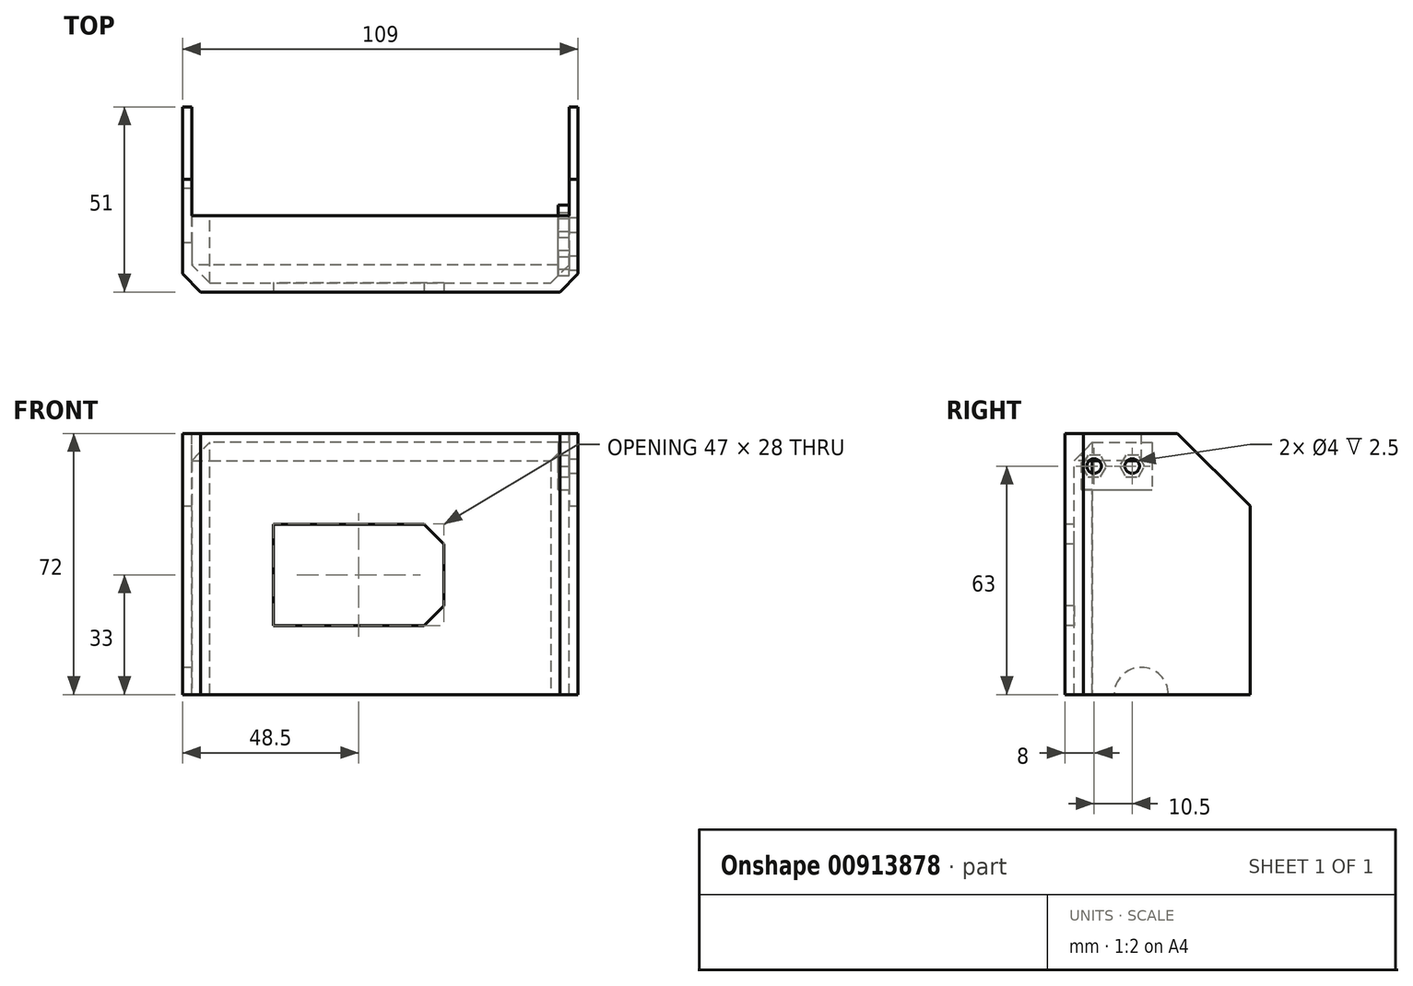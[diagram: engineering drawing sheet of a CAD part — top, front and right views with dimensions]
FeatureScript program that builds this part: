
annotation { "Feature Type Name" : "Feature", "Feature Type Description" : "" }
export const myFeature = defineFeature(function(context is Context, id is Id, definition is map)
    precondition{}
    {
        {
            var Q0;
            Q0=qCreatedBy(makeId("Front.planeOp"),FACE);
            var sketch = newSketch(context, id + "F0", { "sketchPlane" : qUnion([Q0])});
            skLineSegment(sketch, "E0.bottom", {"start": v(0, 0) * mm, "end": v(109, 0) * mm});
            skLineSegment(sketch, "E0.top", {"start": v(0, 72) * mm, "end": v(109, 72) * mm});
            skLineSegment(sketch, "E0.left", {"start": v(0, 0) * mm, "end": v(0, 72) * mm});
            skLineSegment(sketch, "E0.right", {"start": v(109, 0) * mm, "end": v(109, 72) * mm});
            skSolve(sketch);
        }
        {
            var Q0;
            Q0=makeQuery(id+"F0.imprint","IMPRINT",FACE,{"disambiguationData":[TD([[makeQuery(id+"F0.imprint","IMPRINT",EDGE,{"derivedFrom":sQuery(id+"F0.wireOp",EDGE,"E0.bottom")}),1.0]])]});
            extrude(context, id + "F1", {"entities" : qUnion([Q0]), "depth" : 51 * mm, "offsetDistance" : 25 * mm});
        }
        {
            var Q0;
            Q0=makeQuery(id+"F1.opExtrude","CAP_FACE",FACE,{"disambiguationData":[OSD([sQuery(id+"F0.wireOp",EDGE,"E0.bottom"),sQuery(id+"F0.wireOp",EDGE,"E0.top"),sQuery(id+"F0.wireOp",EDGE,"E0.left"),sQuery(id+"F0.wireOp",EDGE,"E0.right")])],"isStart":true});
            shell(context, id + "F2", {"entities" : qUnion([Q0]), "thickness" : 2.5 * mm});
        }
        {
            var Q0;
            Q0=makeQuery(id+"F1.opExtrude","SWEPT_FACE",FACE,{"disambiguationData":[OSD([sQuery(id+"F0.wireOp",EDGE,"E0.top")])]});
            var sketch = newSketch(context, id + "F3", { "sketchPlane" : qUnion([Q0])});
            skLineSegment(sketch, "E1.0.0", {"start": v(109, 0) * mm, "end": v(0, 0) * mm, "construction": true});
            skLineSegment(sketch, "E1.0.1", {"start": v(0, 0) * mm, "end": v(0, -51) * mm, "construction": true});
            skLineSegment(sketch, "E1.0.2", {"start": v(0, -51) * mm, "end": v(109, -51) * mm, "construction": true});
            skLineSegment(sketch, "E1.0.3", {"start": v(109, -51) * mm, "end": v(109, 0) * mm, "construction": true});
            skLineSegment(sketch, "E2.0", {"start": v(2.5, -48.5) * mm, "end": v(2.5, 0) * mm, "construction": true});
            skLineSegment(sketch, "E3.0", {"start": v(106.5, -48.5) * mm, "end": v(106.5, 0) * mm, "construction": true});
            skLineSegment(sketch, "E4.0", {"start": v(2.5, -48.5) * mm, "end": v(106.5, -48.5) * mm, "construction": true});
            skLineSegment(sketch, "E5.bottom", {"start": v(2.5, 0) * mm, "end": v(106.5, 0) * mm});
            skLineSegment(sketch, "E5.top", {"start": v(2.5, -30) * mm, "end": v(106.5, -30) * mm});
            skLineSegment(sketch, "E5.left", {"start": v(2.5, 0) * mm, "end": v(2.5, -30) * mm});
            skLineSegment(sketch, "E5.right", {"start": v(106.5, 0) * mm, "end": v(106.5, -30) * mm});
            skSolve(sketch);
        }
        {
            var Q0;
            Q0=makeQuery(id+"F3.imprint","IMPRINT",FACE,{"disambiguationData":[TD([[makeQuery(id+"F3.imprint","IMPRINT",EDGE,{"derivedFrom":sQuery(id+"F3.wireOp",EDGE,"E5.bottom")}),-1.0]])]});
            var Q1;
            Q1=makeQuery(id+"F2.opShell","OFFSET_FACE",FACE,{"disambiguationData":[OSD([sQuery(id+"F0.wireOp",EDGE,"E0.top")])]});
            extrude(context, id + "F4", {"entities" : qUnion([Q0]), "operationType" : NewBodyOperationType.REMOVE, "endBound" : BoundingType.UP_TO_SURFACE, "oppositeDirection" : true, "depth" : 25 * mm, "endBoundEntityFace" : qUnion([Q1]), "offsetDistance" : 25 * mm});
        }
        {
            var Q0;
            Q0=makeQuery(id+"F1.opExtrude","SWEPT_FACE",FACE,{"disambiguationData":[OSD([sQuery(id+"F0.wireOp",EDGE,"E0.right")])]});
            var sketch = newSketch(context, id + "F5", { "sketchPlane" : qUnion([Q0])});
            skCircle(sketch, "E6", {"center": v(-43, 63) * mm, "radius": 2 * mm});
            skCircle(sketch, "E7", {"center": v(-32.5, 63) * mm, "radius": 2 * mm});
            skLineSegment(sketch, "E8", {"start": v(-43, 63) * mm, "end": v(-32.5, 63) * mm, "construction": true});
            skSolve(sketch);
        }
        {
            var Q0;
            Q0=makeQuery(id+"F5.imprint","IMPRINT",FACE,{"disambiguationData":[TD([[makeQuery(id+"F5.imprint","IMPRINT",EDGE,{"derivedFrom":sQuery(id+"F5.wireOp",EDGE,"E6")}),1.0]])]});
            var Q1;
            Q1=makeQuery(id+"F5.imprint","IMPRINT",FACE,{"disambiguationData":[TD([[makeQuery(id+"F5.imprint","IMPRINT",EDGE,{"derivedFrom":sQuery(id+"F5.wireOp",EDGE,"E7")}),1.0]])]});
            var Q2;
            Q2=makeQuery(id+"F4.boolean.opBoolean","MERGE",FACE,{"derivedFrom":[makeQuery(id+"F2.opShell","OFFSET_FACE",FACE,{"disambiguationData":[OSD([sQuery(id+"F0.wireOp",EDGE,"E0.right")])]})],"fromTools":[makeQuery(id+"F4.opExtrude","SWEPT_FACE",FACE,{"disambiguationData":[OSD([sQuery(id+"F3.wireOp",EDGE,"E5.right")])]})]});
            extrude(context, id + "F6", {"entities" : qUnion([Q0, Q1]), "operationType" : NewBodyOperationType.REMOVE, "endBound" : BoundingType.UP_TO_SURFACE, "oppositeDirection" : true, "depth" : 25 * mm, "endBoundEntityFace" : qUnion([Q2]), "offsetDistance" : 25 * mm});
        }
        {
            var Q0;
            {var subQ0=sQuery(id+"F0.wireOp",EDGE,"E0.right");var subQ1=sQuery(id+"F0.wireOp",EDGE,"E0.top");Q0=makeQuery(id+"F4.boolean.opBoolean","SPLIT",EDGE,{"disambiguationData":[TD([makeQuery(id+"F1.opExtrude","SWEPT_FACE",FACE,{"disambiguationData":[OSD([subQ0])]})])],"derivedFrom":makeQuery(id+"F1.opExtrude","CAP_EDGE",EDGE,{"disambiguationData":[OSD([subQ1])],"isStart":true})});}
            var Q1;
            {var subQ0=sQuery(id+"F0.wireOp",EDGE,"E0.left");var subQ1=sQuery(id+"F0.wireOp",EDGE,"E0.top");Q1=makeQuery(id+"F4.boolean.opBoolean","SPLIT",EDGE,{"disambiguationData":[TD([makeQuery(id+"F1.opExtrude","SWEPT_FACE",FACE,{"disambiguationData":[OSD([subQ0])]})])],"derivedFrom":makeQuery(id+"F1.opExtrude","CAP_EDGE",EDGE,{"disambiguationData":[OSD([subQ1])],"isStart":true})});}
            chamfer(context, id + "F7", {"entities" : qUnion([Q0, Q1]), "width" : 20 * mm, "tangentPropagation" : true});
        }
        {
            var Q0;
            Q0=makeQuery(id+"F1.opExtrude","SWEPT_FACE",FACE,{"disambiguationData":[OSD([sQuery(id+"F0.wireOp",EDGE,"E0.bottom")])]});
            var sketch = newSketch(context, id + "F8", { "sketchPlane" : qUnion([Q0])});
            skLineSegment(sketch, "E9.0.0", {"start": v(106.5, 0) * mm, "end": v(2.5, 0) * mm, "construction": true});
            skLineSegment(sketch, "E9.0.1", {"start": v(2.5, 0) * mm, "end": v(2.5, 48.5) * mm, "construction": true});
            skLineSegment(sketch, "E9.0.2", {"start": v(2.5, 48.5) * mm, "end": v(106.5, 48.5) * mm, "construction": true});
            skLineSegment(sketch, "E9.0.3", {"start": v(106.5, 48.5) * mm, "end": v(106.5, 0) * mm, "construction": true});
            skLineSegment(sketch, "E10.0.0", {"start": v(0, 0) * mm, "end": v(109, 0) * mm, "construction": true});
            skLineSegment(sketch, "E10.0.1", {"start": v(109, 0) * mm, "end": v(109, 51) * mm, "construction": true});
            skLineSegment(sketch, "E10.0.2", {"start": v(109, 51) * mm, "end": v(0, 51) * mm, "construction": true});
            skLineSegment(sketch, "E10.0.3", {"start": v(0, 51) * mm, "end": v(0, 0) * mm, "construction": true});
            skLineSegment(sketch, "E11.bottom", {"start": v(2.5, 0) * mm, "end": v(106.5, 0) * mm});
            skLineSegment(sketch, "E11.top", {"start": v(2.5, 48.5) * mm, "end": v(106.5, 48.5) * mm});
            skLineSegment(sketch, "E11.left", {"start": v(2.5, 0) * mm, "end": v(2.5, 48.5) * mm});
            skLineSegment(sketch, "E11.right", {"start": v(106.5, 0) * mm, "end": v(106.5, 48.5) * mm});
            skSolve(sketch);
        }
        {
            var Q0;
            Q0=makeQuery(id+"F8.imprint","IMPRINT",FACE,{"disambiguationData":[TD([[makeQuery(id+"F8.imprint","IMPRINT",EDGE,{"derivedFrom":sQuery(id+"F8.wireOp",EDGE,"E11.bottom")}),1.0]])]});
            var Q1;
            Q1=makeQuery(id+"F2.opShell","OFFSET_FACE",FACE,{"disambiguationData":[OSD([sQuery(id+"F0.wireOp",EDGE,"E0.bottom")])]});
            extrude(context, id + "F9", {"entities" : qUnion([Q0]), "operationType" : NewBodyOperationType.REMOVE, "endBound" : BoundingType.UP_TO_SURFACE, "oppositeDirection" : true, "depth" : 25 * mm, "endBoundEntityFace" : qUnion([Q1]), "offsetDistance" : 25 * mm});
        }
        {
            var Q0;
            Q0=makeQuery(id+"F1.opExtrude","SWEPT_FACE",FACE,{"disambiguationData":[OSD([sQuery(id+"F0.wireOp",EDGE,"E0.left")])]});
            var sketch = newSketch(context, id + "F10", { "sketchPlane" : qUnion([Q0])});
            skCircle(sketch, "E12", {"center": v(30, 0) * mm, "radius": 7.5 * mm});
            skSolve(sketch);
        }
        {
            var Q0;
            {var subQ0=sQuery(id+"F10.wireOp",EDGE,"E12");var subQ1=makeQuery(id+"F1.opExtrude","SWEPT_EDGE",EDGE,{"disambiguationData":[OSD([sQuery(id+"F0.wireOp",EDGE,"E0.bottom"),sQuery(id+"F0.wireOp",EDGE,"E0.left")])]});var subQ2=makeQuery(id+"F10.imprint","INTERSECT",VERTEX,{"disambiguationData":[OD(0.0)],"derivedFrom":[subQ1,subQ0]});Q0=makeQuery(id+"F10.imprint","IMPRINT",FACE,{"disambiguationData":[TD([[makeQuery(id+"F10.imprint","IMPRINT",EDGE,{"disambiguationData":[TD([[subQ2,1.0]])],"derivedFrom":subQ0}),1.0]])]});}
            var Q1;
            Q1=makeQuery(id+"F9.boolean.opBoolean","MERGE",FACE,{"derivedFrom":[makeQuery(id+"F4.boolean.opBoolean","MERGE",FACE,{"derivedFrom":[makeQuery(id+"F2.opShell","OFFSET_FACE",FACE,{"disambiguationData":[OSD([sQuery(id+"F0.wireOp",EDGE,"E0.left")])]})],"fromTools":[makeQuery(id+"F4.opExtrude","SWEPT_FACE",FACE,{"disambiguationData":[OSD([sQuery(id+"F3.wireOp",EDGE,"E5.left")])]})]})],"fromTools":[makeQuery(id+"F9.opExtrude","SWEPT_FACE",FACE,{"disambiguationData":[OSD([sQuery(id+"F8.wireOp",EDGE,"E11.left")])]})]});
            extrude(context, id + "F11", {"entities" : qUnion([Q0]), "operationType" : NewBodyOperationType.REMOVE, "endBound" : BoundingType.UP_TO_SURFACE, "oppositeDirection" : true, "depth" : 25 * mm, "endBoundEntityFace" : qUnion([Q1]), "offsetDistance" : 25 * mm});
        }
        {
            var Q0;
            Q0=makeQuery(id+"F1.opExtrude","CAP_FACE",FACE,{"disambiguationData":[OSD([sQuery(id+"F0.wireOp",EDGE,"E0.bottom"),sQuery(id+"F0.wireOp",EDGE,"E0.top"),sQuery(id+"F0.wireOp",EDGE,"E0.left"),sQuery(id+"F0.wireOp",EDGE,"E0.right")])],"isStart":false});
            var sketch = newSketch(context, id + "F12", { "sketchPlane" : qUnion([Q0])});
            skLineSegment(sketch, "E13.bottom", {"start": v(25, 47) * mm, "end": v(72, 47) * mm});
            skLineSegment(sketch, "E13.top", {"start": v(25, 19) * mm, "end": v(72, 19) * mm});
            skLineSegment(sketch, "E13.left", {"start": v(25, 47) * mm, "end": v(25, 19) * mm});
            skLineSegment(sketch, "E13.right", {"start": v(72, 47) * mm, "end": v(72, 19) * mm});
            skLineSegment(sketch, "E14", {"start": v(66.5, 47) * mm, "end": v(72, 41.5) * mm});
            skLineSegment(sketch, "E15", {"start": v(25, 33) * mm, "end": v(72, 33) * mm, "construction": true});
            skLineSegment(sketch, "E16.MirrorCS", {"start": v(66.5, 19) * mm, "end": v(72, 24.5) * mm});
            skSolve(sketch);
        }
        {
            var Q0;
            Q0=makeQuery(id+"F9.boolean.opBoolean","MERGE",FACE,{"derivedFrom":[makeQuery(id+"F4.boolean.opBoolean","MERGE",FACE,{"derivedFrom":[makeQuery(id+"F2.opShell","OFFSET_FACE",FACE,{"disambiguationData":[OSD([sQuery(id+"F0.wireOp",EDGE,"E0.right")])]})],"fromTools":[makeQuery(id+"F4.opExtrude","SWEPT_FACE",FACE,{"disambiguationData":[OSD([sQuery(id+"F3.wireOp",EDGE,"E5.right")])]})]})],"fromTools":[makeQuery(id+"F9.opExtrude","SWEPT_FACE",FACE,{"disambiguationData":[OSD([sQuery(id+"F8.wireOp",EDGE,"E11.right")])]})]});
            var sketch = newSketch(context, id + "F13", { "sketchPlane" : qUnion([Q0])});
            skLineSegment(sketch, "E17.bottom", {"start": v(48.5, 69.5) * mm, "end": v(27, 69.5) * mm});
            skLineSegment(sketch, "E17.top", {"start": v(48.5, 56.5) * mm, "end": v(27, 56.5) * mm});
            skLineSegment(sketch, "E17.left", {"start": v(48.5, 69.5) * mm, "end": v(48.5, 56.5) * mm});
            skLineSegment(sketch, "E17.right", {"start": v(27, 69.5) * mm, "end": v(27, 56.5) * mm});
            skCircle(sketch, "E18.0", {"center": v(32.5, 63) * mm, "radius": 2 * mm, "construction": true});
            skCircle(sketch, "E19.0", {"center": v(43, 63) * mm, "radius": 2 * mm, "construction": true});
            skCircle(sketch, "E20.cCircle", {"center": v(32.5, 63) * mm, "radius": 3 * mm, "construction": true});
            skLineSegment(sketch, "E20.0", {"start": v(30.77, 66) * mm, "end": v(34.23, 66) * mm});
            skLineSegment(sketch, "E20.1", {"start": v(34.23, 66) * mm, "end": v(35.96, 63) * mm});
            skLineSegment(sketch, "E20.2", {"start": v(35.96, 63) * mm, "end": v(34.23, 60) * mm});
            skLineSegment(sketch, "E20.3", {"start": v(34.23, 60) * mm, "end": v(30.77, 60) * mm});
            skLineSegment(sketch, "E20.4", {"start": v(30.77, 60) * mm, "end": v(29.04, 63) * mm});
            skLineSegment(sketch, "E20.5", {"start": v(29.04, 63) * mm, "end": v(30.77, 66) * mm});
            skPoint(sketch, "E20.0.midPoint", {"position": v(32.5, 66) * mm});
            skCircle(sketch, "E21.cCircle", {"center": v(43, 63) * mm, "radius": 3 * mm, "construction": true});
            skLineSegment(sketch, "E21.0", {"start": v(41.27, 66) * mm, "end": v(44.73, 66) * mm});
            skLineSegment(sketch, "E21.1", {"start": v(44.73, 66) * mm, "end": v(46.46, 63) * mm});
            skLineSegment(sketch, "E21.2", {"start": v(46.46, 63) * mm, "end": v(44.73, 60) * mm});
            skLineSegment(sketch, "E21.3", {"start": v(44.73, 60) * mm, "end": v(41.27, 60) * mm});
            skLineSegment(sketch, "E21.4", {"start": v(41.27, 60) * mm, "end": v(39.54, 63) * mm});
            skLineSegment(sketch, "E21.5", {"start": v(39.54, 63) * mm, "end": v(41.27, 66) * mm});
            skPoint(sketch, "E21.0.midPoint", {"position": v(43, 66) * mm});
            skLineSegment(sketch, "E22", {"start": v(29.04, 63) * mm, "end": v(27, 63) * mm, "construction": true});
            skLineSegment(sketch, "E23", {"start": v(46.46, 63) * mm, "end": v(48.5, 63) * mm, "construction": true});
            skSolve(sketch);
        }
        {
            var Q0;
            Q0=makeQuery(id+"F13.imprint","IMPRINT",FACE,{"disambiguationData":[TD([[makeQuery(id+"F13.imprint","IMPRINT",EDGE,{"derivedFrom":sQuery(id+"F13.wireOp",EDGE,"E17.top")}),-1.0]])]});
            extrude(context, id + "F14", {"entities" : qUnion([Q0]), "operationType" : NewBodyOperationType.ADD, "depth" : 3 * mm, "offsetDistance" : 25 * mm});
        }
        {
            var Q0;
            {var subQ3=sQuery(id+"F12.wireOp",EDGE,"E13.left");Q0=makeQuery(id+"F12.imprint","IMPRINT",FACE,{"disambiguationData":[TD([[makeQuery(id+"F12.imprint","IMPRINT",EDGE,{"derivedFrom":subQ3}),1.0]])]});}
            var Q1;
            Q1=makeQuery(id+"F9.boolean.opBoolean","MERGE",FACE,{"derivedFrom":[makeQuery(id+"F2.opShell","OFFSET_FACE",FACE,{"disambiguationData":[OSD([sQuery(id+"F0.wireOp",EDGE,"E0.bottom"),sQuery(id+"F0.wireOp",EDGE,"E0.top"),sQuery(id+"F0.wireOp",EDGE,"E0.left"),sQuery(id+"F0.wireOp",EDGE,"E0.right")])]})],"fromTools":[makeQuery(id+"F9.opExtrude","SWEPT_FACE",FACE,{"disambiguationData":[OSD([sQuery(id+"F8.wireOp",EDGE,"E11.top")])]})]});
            extrude(context, id + "F15", {"entities" : qUnion([Q0]), "operationType" : NewBodyOperationType.REMOVE, "endBound" : BoundingType.UP_TO_SURFACE, "oppositeDirection" : true, "depth" : 25 * mm, "endBoundEntityFace" : qUnion([Q1]), "offsetDistance" : 25 * mm});
        }
        {
            var Q0;
            {var subQ0=sQuery(id+"F0.wireOp",EDGE,"E0.left");Q0=makeQuery(id+"F9.boolean.opBoolean","MERGE",EDGE,{"derivedFrom":[makeQuery(id+"F2.opShell","OFFSET_EDGE",EDGE,{"disambiguationData":[OSD([subQ0]),TDD([makeQuery(id+"F1.opExtrude","CAP_EDGE",EDGE,{"disambiguationData":[OSD([subQ0])],"isStart":false})])]})],"fromTools":[makeQuery(id+"F9.opExtrude","SWEPT_EDGE",EDGE,{"disambiguationData":[OSD([sQuery(id+"F8.wireOp",EDGE,"E11.top"),sQuery(id+"F8.wireOp",EDGE,"E11.left")])]})]});}
            var Q1;
            Q1=makeQuery(id+"F2.opShell","OFFSET_EDGE",EDGE,{"disambiguationData":[OSD([sQuery(id+"F0.wireOp",EDGE,"E0.top"),sQuery(id+"F0.wireOp",EDGE,"E0.left")])]});
            var Q2;
            {var subQ0=sQuery(id+"F0.wireOp",EDGE,"E0.top");Q2=makeQuery(id+"F2.opShell","OFFSET_EDGE",EDGE,{"disambiguationData":[OSD([subQ0]),TDD([makeQuery(id+"F1.opExtrude","CAP_EDGE",EDGE,{"disambiguationData":[OSD([subQ0])],"isStart":false})])]});}
            var Q3;
            {var subQ0=sQuery(id+"F0.wireOp",EDGE,"E0.right");Q3=makeQuery(id+"F9.boolean.opBoolean","MERGE",EDGE,{"derivedFrom":[makeQuery(id+"F2.opShell","OFFSET_EDGE",EDGE,{"disambiguationData":[OSD([subQ0]),TDD([makeQuery(id+"F1.opExtrude","CAP_EDGE",EDGE,{"disambiguationData":[OSD([subQ0])],"isStart":false})])]})],"fromTools":[makeQuery(id+"F9.opExtrude","SWEPT_EDGE",EDGE,{"disambiguationData":[OSD([sQuery(id+"F8.wireOp",EDGE,"E11.top"),sQuery(id+"F8.wireOp",EDGE,"E11.right")])]})]});}
            chamfer(context, id + "F16", {"entities" : qUnion([Q0, Q1, Q2, Q3]), "width" : 5 * mm, "tangentPropagation" : true});
        }
        {
            var Q0;
            Q0=makeQuery(id+"F1.opExtrude","CAP_EDGE",EDGE,{"disambiguationData":[OSD([sQuery(id+"F0.wireOp",EDGE,"E0.left")])],"isStart":false});
            var Q1;
            Q1=makeQuery(id+"F1.opExtrude","CAP_EDGE",EDGE,{"disambiguationData":[OSD([sQuery(id+"F0.wireOp",EDGE,"E0.right")])],"isStart":false});
            chamfer(context, id + "F17", {"entities" : qUnion([Q0, Q1]), "width" : 5 * mm, "tangentPropagation" : true});
        }
    });
